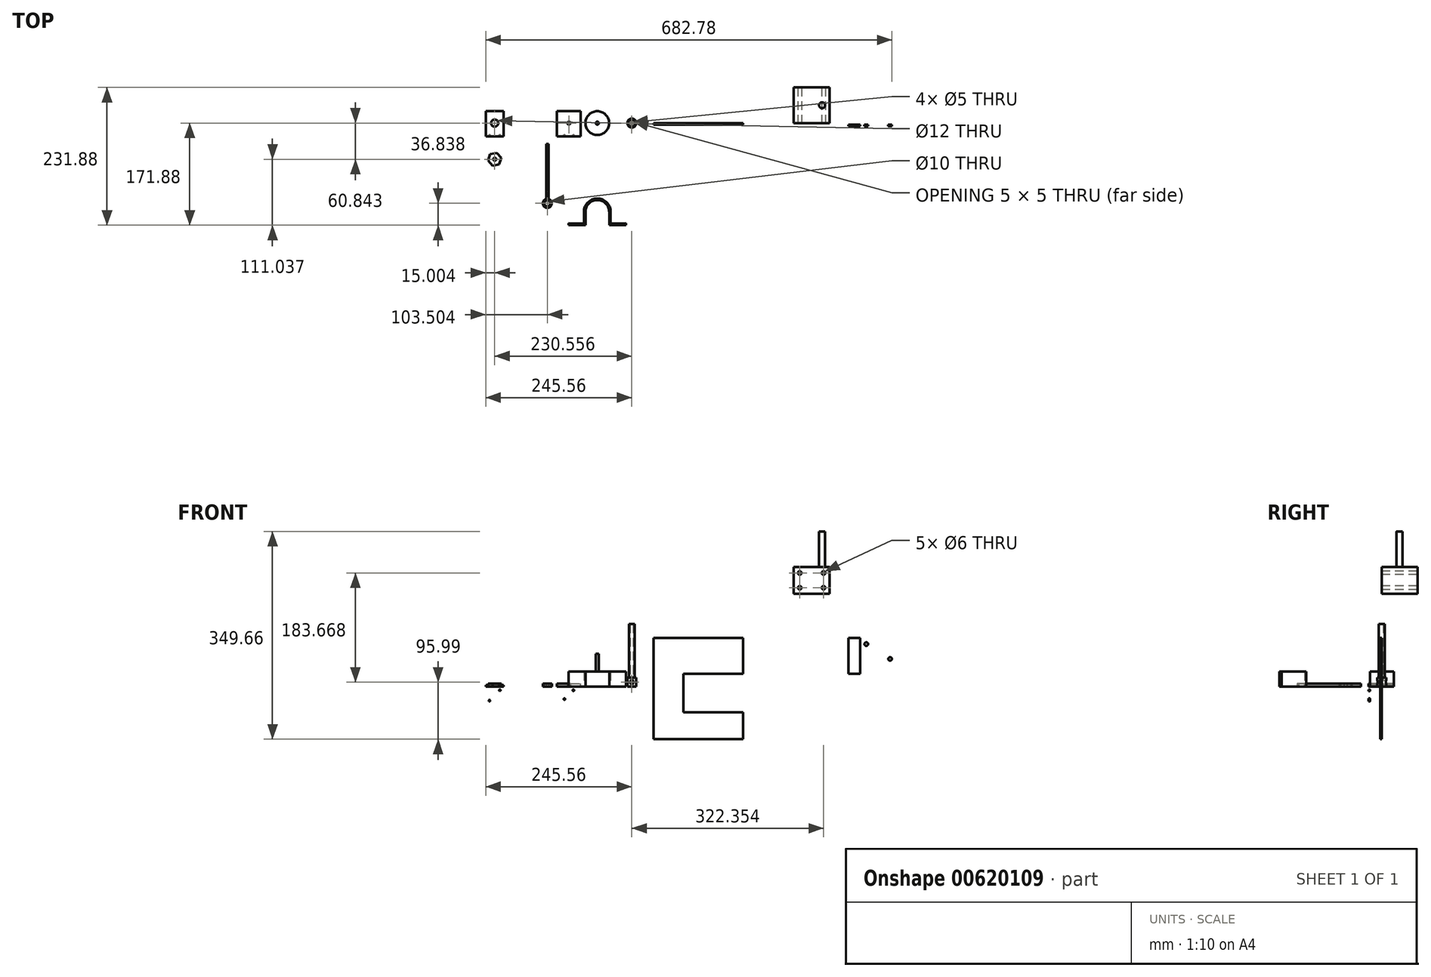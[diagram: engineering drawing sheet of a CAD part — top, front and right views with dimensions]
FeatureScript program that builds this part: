
annotation { "Feature Type Name" : "Feature", "Feature Type Description" : "" }
export const myFeature = defineFeature(function(context is Context, id is Id, definition is map)
    precondition{}
    {
        {
            var Q0;
            Q0=qCreatedBy(makeId("Top.planeOp"),FACE);
            var sketch = newSketch(context, id + "F0", { "sketchPlane" : qUnion([Q0])});
            skCircle(sketch, "E0", {"center": v(0, 0) * mm, "radius": 2.5 * mm});
            skCircle(sketch, "E1", {"center": v(0, 0) * mm, "radius": 7.5 * mm});
            skLineSegment(sketch, "E2", {"start": v(-20, 7.5) * mm, "end": v(20, 7.5) * mm});
            skCircle(sketch, "E3", {"center": v(-57.97, 0) * mm, "radius": 20 * mm});
            skLineSegment(sketch, "E4.bottom", {"start": v(-125.74, 20) * mm, "end": v(-85.74, 20) * mm});
            skLineSegment(sketch, "E4.top", {"start": v(-125.74, -20) * mm, "end": v(-85.74, -20) * mm});
            skLineSegment(sketch, "E4.left", {"start": v(-125.74, 20) * mm, "end": v(-125.74, -20) * mm});
            skLineSegment(sketch, "E4.right", {"start": v(-85.74, 20) * mm, "end": v(-85.74, -20) * mm});
            skPoint(sketch, "E4.middle", {"position": v(-105.74, 0) * mm});
            skCircle(sketch, "E5", {"center": v(-105.74, 0) * mm, "radius": 2.5 * mm});
            skLineSegment(sketch, "E6.bottom", {"start": v(-215.56, 20) * mm, "end": v(-245.56, 20) * mm});
            skLineSegment(sketch, "E6.top", {"start": v(-215.56, -20) * mm, "end": v(-245.56, -20) * mm});
            skLineSegment(sketch, "E6.left", {"start": v(-215.56, 20) * mm, "end": v(-215.56, -20) * mm});
            skLineSegment(sketch, "E6.right", {"start": v(-245.56, 20) * mm, "end": v(-245.56, -20) * mm});
            skCircle(sketch, "E7", {"center": v(-230.56, 0) * mm, "radius": 6 * mm});
            skPoint(sketch, "E7.centerSnap0", {"position": v(-230.56, 20) * mm});
            skCircle(sketch, "E8.cCircle", {"center": v(-230.56, -60.84) * mm, "radius": 9.88 * mm, "construction": true});
            skLineSegment(sketch, "E8.0", {"start": v(-219.4, -58.45) * mm, "end": v(-222.9, -69.3) * mm});
            skLineSegment(sketch, "E8.1", {"start": v(-222.9, -69.3) * mm, "end": v(-234.06, -71.7) * mm});
            skLineSegment(sketch, "E8.2", {"start": v(-234.06, -71.7) * mm, "end": v(-241.71, -63.24) * mm});
            skLineSegment(sketch, "E8.3", {"start": v(-241.71, -63.24) * mm, "end": v(-238.21, -52.38) * mm});
            skLineSegment(sketch, "E8.4", {"start": v(-238.21, -52.38) * mm, "end": v(-227.05, -49.98) * mm});
            skLineSegment(sketch, "E8.5", {"start": v(-227.05, -49.98) * mm, "end": v(-219.4, -58.45) * mm});
            skPoint(sketch, "E8.0.midPoint", {"position": v(-221.15, -63.88) * mm});
            skCircle(sketch, "E9", {"center": v(-230.56, -60.84) * mm, "radius": 2.5 * mm});
            skCircle(sketch, "E10", {"center": v(-142.06, -135.04) * mm, "radius": 5 * mm});
            skArc(sketch, "E11", {"start": v(-144.06, -127.81) * mm, "mid": v(-142.06, -142.54) * mm, "end": v(-140.06, -127.81) * mm});
            skLineSegment(sketch, "E12", {"start": v(-140.06, -127.81) * mm, "end": v(-140.06, -35.04) * mm});
            skLineSegment(sketch, "E13", {"start": v(-140.06, -35.04) * mm, "end": v(-142.06, -35.04) * mm});
            skLineSegment(sketch, "E14.MirrorCS", {"start": v(-144.06, -127.81) * mm, "end": v(-144.06, -35.04) * mm});
            skLineSegment(sketch, "E15", {"start": v(-142.06, -35.04) * mm, "end": v(-144.06, -35.04) * mm});
            skArc(sketch, "E16", {"start": v(-35.47, -149.38) * mm, "mid": v(-57.97, -126.88) * mm, "end": v(-80.47, -149.38) * mm});
            skLineSegment(sketch, "E17", {"start": v(-80.47, -149.38) * mm, "end": v(-80.47, -168.95) * mm});
            skLineSegment(sketch, "E18", {"start": v(-80.47, -171.88) * mm, "end": v(-106.45, -171.88) * mm});
            skLineSegment(sketch, "E19", {"start": v(-106.45, -171.88) * mm, "end": v(-106.45, -168.45) * mm});
            skLineSegment(sketch, "E20", {"start": v(-106.45, -168.45) * mm, "end": v(-80.47, -168.95) * mm});
            skLineSegment(sketch, "E21", {"start": v(-77.97, -149.38) * mm, "end": v(-77.97, -171.88) * mm});
            skLineSegment(sketch, "E22", {"start": v(-77.97, -171.88) * mm, "end": v(-80.47, -171.88) * mm});
            skLineSegment(sketch, "E23.MirrorCS", {"start": v(-37.97, -149.38) * mm, "end": v(-37.97, -171.88) * mm});
            skLineSegment(sketch, "E24.MirrorCS", {"start": v(-35.47, -149.38) * mm, "end": v(-35.47, -168.95) * mm});
            skLineSegment(sketch, "E25.MirrorCS", {"start": v(-9.5, -168.45) * mm, "end": v(-35.47, -168.95) * mm});
            skLineSegment(sketch, "E26.MirrorCS", {"start": v(-9.5, -171.88) * mm, "end": v(-9.5, -168.45) * mm});
            skLineSegment(sketch, "E27.MirrorCS", {"start": v(-35.47, -171.88) * mm, "end": v(-9.5, -171.88) * mm});
            skLineSegment(sketch, "E28.MirrorCS", {"start": v(-37.97, -171.88) * mm, "end": v(-35.47, -171.88) * mm});
            skArc(sketch, "E29.trimOffspring", {"start": v(-37.97, -149.38) * mm, "mid": v(-57.97, -129.38) * mm, "end": v(-77.97, -149.38) * mm});
            skLineSegment(sketch, "E30", {"start": v(-57.97, -130.48) * mm, "end": v(-57.98, -130.48) * mm});
            skLineSegment(sketch, "E31", {"start": v(-57.97, -126.88) * mm, "end": v(-80.26, -126.88) * mm, "construction": true});
            skPoint(sketch, "E32.start.orphan", {"position": v(-57.97, -129.38) * mm});
            skLineSegment(sketch, "E33.MirrorCS", {"start": v(-57.98, -130.48) * mm, "end": v(-57.97, -130.48) * mm});
            skPoint(sketch, "E34.end.orphan", {"position": v(-57.97, -133.51) * mm});
            skLineSegment(sketch, "E35.trimOffspring", {"start": v(-51.44, -130.48) * mm, "end": v(-51.38, -130.48) * mm});
            skSolve(sketch);
        }
        {
            var Q0;
            Q0=makeQuery(id+"F0.imprint","IMPRINT",FACE,{"disambiguationData":[TD([[makeQuery(id+"F0.imprint","IMPRINT",EDGE,{"derivedFrom":sQuery(id+"F0.wireOp",EDGE,"E0")}),-1.0]])]});
            extrude(context, id + "F1", {"entities" : qUnion([Q0]), "depth" : 15 * mm, "offsetDistance" : 25 * mm});
        }
        {
            var Q0;
            Q0=makeQuery(id+"F1.opExtrude","CAP_FACE",FACE,{"disambiguationData":[OSD([sQuery(id+"F0.wireOp",EDGE,"E0"),sQuery(id+"F0.wireOp",EDGE,"E1")])],"isStart":false});
            var sketch = newSketch(context, id + "F2", { "sketchPlane" : qUnion([Q0])});
            skCircle(sketch, "E36", {"center": v(0, 0) * mm, "radius": 5 * mm});
            skSolve(sketch);
        }
        {
            var Q0;
            Q0=makeQuery(id+"F2.imprint","IMPRINT",FACE,{"disambiguationData":[TD([[makeQuery(id+"F2.imprint","IMPRINT",EDGE,{"derivedFrom":sQuery(id+"F2.wireOp",EDGE,"E36")}),1.0]])]});
            extrude(context, id + "F3", {"entities" : qUnion([Q0]), "operationType" : NewBodyOperationType.ADD, "depth" : 90 * mm, "offsetDistance" : 25 * mm});
        }
        {
            var Q0;
            Q0=sQuery(id+"F0.wireOp",EDGE,"E2");
            extrude(context, id + "F4", {"bodyType" : ToolBodyType.SURFACE, "surfaceEntities" : qUnion([Q0]), "depth" : 15 * mm, "offsetDistance" : 25 * mm});
        }
        {
            var Q0;
            Q0=makeQuery(id+"F4.opExtrude","SWEPT_FACE",FACE,{"disambiguationData":[OSD([sQuery(id+"F0.wireOp",EDGE,"E2")])]});
            var sketch = newSketch(context, id + "F5", { "sketchPlane" : qUnion([Q0])});
            skCircle(sketch, "E37", {"center": v(0, 7.5) * mm, "radius": 3 * mm});
            skPoint(sketch, "E37.centerSnap0", {"position": v(-20, 7.5) * mm});
            skSolve(sketch);
        }
        {
            var Q0;
            Q0=makeQuery(id+"F5.imprint","IMPRINT",FACE,{"disambiguationData":[TD([[makeQuery(id+"F5.imprint","IMPRINT",EDGE,{"derivedFrom":sQuery(id+"F5.wireOp",EDGE,"E37")}),1.0]])]});
            extrude(context, id + "F6", {"entities" : qUnion([Q0]), "operationType" : NewBodyOperationType.REMOVE, "endBound" : BoundingType.THROUGH_ALL, "depth" : 25 * mm, "offsetDistance" : 25 * mm});
        }
        {
            var Q0;
            Q0=makeQuery(id+"F0.imprint","IMPRINT",FACE,{"disambiguationData":[TD([[makeQuery(id+"F0.imprint","IMPRINT",EDGE,{"derivedFrom":sQuery(id+"F0.wireOp",EDGE,"E3")}),1.0]])]});
            extrude(context, id + "F7", {"entities" : qUnion([Q0]), "depth" : 25 * mm, "offsetDistance" : 25 * mm});
        }
        {
            var Q0;
            Q0=makeQuery(id+"F7.opExtrude","CAP_FACE",FACE,{"disambiguationData":[OSD([sQuery(id+"F0.wireOp",EDGE,"E3")])],"isStart":false});
            var sketch = newSketch(context, id + "F8", { "sketchPlane" : qUnion([Q0])});
            skCircle(sketch, "E38", {"center": v(-57.97, 0) * mm, "radius": 2.5 * mm});
            skSolve(sketch);
        }
        {
            var Q0;
            Q0=makeQuery(id+"F8.imprint","IMPRINT",FACE,{"disambiguationData":[TD([[makeQuery(id+"F8.imprint","IMPRINT",EDGE,{"derivedFrom":sQuery(id+"F8.wireOp",EDGE,"E38")}),1.0]])]});
            extrude(context, id + "F9", {"entities" : qUnion([Q0]), "operationType" : NewBodyOperationType.ADD, "depth" : 30 * mm, "offsetDistance" : 25 * mm});
        }
        {
            var Q0;
            Q0=makeQuery(id+"F0.imprint","IMPRINT",FACE,{"disambiguationData":[TD([[makeQuery(id+"F0.imprint","IMPRINT",EDGE,{"derivedFrom":sQuery(id+"F0.wireOp",EDGE,"E4.bottom")}),-1.0]])]});
            extrude(context, id + "F10", {"entities" : qUnion([Q0]), "depth" : 5 * mm, "offsetDistance" : 25 * mm});
        }
        {
            var Q0;
            Q0=makeQuery(id+"F10.opExtrude","CAP_FACE",FACE,{"disambiguationData":[OSD([sQuery(id+"F0.wireOp",EDGE,"E4.bottom"),sQuery(id+"F0.wireOp",EDGE,"E4.top"),sQuery(id+"F0.wireOp",EDGE,"E4.left"),sQuery(id+"F0.wireOp",EDGE,"E4.right"),sQuery(id+"F0.wireOp",EDGE,"E5")])],"isStart":false});
            var sketch = newSketch(context, id + "F11", { "sketchPlane" : qUnion([Q0])});
            skLineSegment(sketch, "E39.bottom", {"start": v(-125.74, -20) * mm, "end": v(-85.74, -20) * mm});
            skLineSegment(sketch, "E39.top", {"start": v(-125.74, -22.5) * mm, "end": v(-85.74, -22.5) * mm});
            skLineSegment(sketch, "E39.left", {"start": v(-125.74, -20) * mm, "end": v(-125.74, -22.5) * mm});
            skLineSegment(sketch, "E39.right", {"start": v(-85.74, -20) * mm, "end": v(-85.74, -22.5) * mm});
            skSolve(sketch);
        }
        {
            var Q0;
            Q0=makeQuery(id+"F11.imprint","IMPRINT",FACE,{"disambiguationData":[TD([[makeQuery(id+"F11.imprint","IMPRINT",EDGE,{"derivedFrom":sQuery(id+"F11.wireOp",EDGE,"E39.bottom")}),-1.0]])]});
            extrude(context, id + "F12", {"entities" : qUnion([Q0]), "operationType" : NewBodyOperationType.ADD, "oppositeDirection" : true, "depth" : 32.5 * mm, "offsetDistance" : 25 * mm});
        }
        {
            var Q0;
            Q0=qCreatedBy(makeId("Front.planeOp"),FACE);
            var sketch = newSketch(context, id + "F13", { "sketchPlane" : qUnion([Q0])});
            skLineSegment(sketch, "E40.bottom", {"start": v(36.88, 81.5) * mm, "end": v(186.88, 81.5) * mm});
            skLineSegment(sketch, "E40.top", {"start": v(36.88, -88.5) * mm, "end": v(186.88, -88.5) * mm});
            skLineSegment(sketch, "E40.left", {"start": v(36.88, 81.5) * mm, "end": v(36.88, -88.5) * mm});
            skLineSegment(sketch, "E40.right", {"start": v(186.88, 81.5) * mm, "end": v(186.88, -88.5) * mm});
            skLineSegment(sketch, "E41", {"start": v(186.88, 21.5) * mm, "end": v(86.88, 21.5) * mm});
            skLineSegment(sketch, "E42", {"start": v(186.88, -43.5) * mm, "end": v(86.88, -43.5) * mm});
            skLineSegment(sketch, "E43", {"start": v(86.88, 21.5) * mm, "end": v(86.88, -43.5) * mm});
            skLineSegment(sketch, "E44.bottom", {"start": v(272.35, 201.17) * mm, "end": v(332.35, 201.17) * mm});
            skLineSegment(sketch, "E44.top", {"start": v(272.35, 156.17) * mm, "end": v(332.35, 156.17) * mm});
            skLineSegment(sketch, "E44.left", {"start": v(272.35, 201.17) * mm, "end": v(272.35, 156.17) * mm});
            skLineSegment(sketch, "E44.right", {"start": v(332.35, 201.17) * mm, "end": v(332.35, 156.17) * mm});
            skCircle(sketch, "E45", {"center": v(322.35, 191.17) * mm, "radius": 3 * mm});
            skLineSegment(sketch, "E46", {"start": v(272.35, 178.67) * mm, "end": v(332.35, 178.67) * mm, "construction": true});
            skLineSegment(sketch, "E47", {"start": v(302.35, 156.17) * mm, "end": v(302.35, 201.17) * mm, "construction": true});
            skCircle(sketch, "E48.MirrorC", {"center": v(282.35, 191.17) * mm, "radius": 3 * mm});
            skCircle(sketch, "E49.MirrorC", {"center": v(282.35, 166.17) * mm, "radius": 3 * mm});
            skCircle(sketch, "E50.MirrorC", {"center": v(322.35, 166.17) * mm, "radius": 3 * mm});
            skSolve(sketch);
        }
        {
            var Q0;
            {var subQ1=sQuery(id+"F13.wireOp",EDGE,"E40.bottom");Q0=makeQuery(id+"F13.imprint","IMPRINT",FACE,{"disambiguationData":[TD([[makeQuery(id+"F13.imprint","IMPRINT",EDGE,{"derivedFrom":subQ1}),-1.0]])]});}
            extrude(context, id + "F14", {"entities" : qUnion([Q0]), "depth" : 2.5 * mm, "offsetDistance" : 25 * mm});
        }
        {
            var Q0;
            Q0=makeQuery(id+"F14.opExtrude","CAP_FACE",FACE,{"disambiguationData":[OSD([sQuery(id+"F13.wireOp",EDGE,"E40.bottom"),sQuery(id+"F13.wireOp",EDGE,"E40.top"),sQuery(id+"F13.wireOp",EDGE,"E40.left"),sQuery(id+"F13.wireOp",EDGE,"E40.right"),sQuery(id+"F13.wireOp",EDGE,"E41"),sQuery(id+"F13.wireOp",EDGE,"E42"),sQuery(id+"F13.wireOp",EDGE,"E43")])],"isStart":false});
            var sketch = newSketch(context, id + "F15", { "sketchPlane" : qUnion([Q0])});
            skLineSegment(sketch, "E51", {"start": v(186.88, 49) * mm, "end": v(86.88, 49) * mm});
            skLineSegment(sketch, "E52", {"start": v(86.88, 49) * mm, "end": v(86.88, 21.5) * mm});
            skLineSegment(sketch, "E53", {"start": v(186.88, -43.5) * mm, "end": v(86.88, -43.5) * mm});
            skLineSegment(sketch, "E54", {"start": v(86.88, -43.5) * mm, "end": v(86.88, -43.5) * mm});
            skLineSegment(sketch, "E55", {"start": v(86.88, 49) * mm, "end": v(86.88, 81.5) * mm});
            skLineSegment(sketch, "E56", {"start": v(86.88, 81.5) * mm, "end": v(86.88, -88.5) * mm});
            skLineSegment(sketch, "E57.bottom", {"start": v(364.22, 81.5) * mm, "end": v(444.22, 81.5) * mm});
            skLineSegment(sketch, "E57.top", {"start": v(384.22, 36.5) * mm, "end": v(444.22, 36.5) * mm});
            skLineSegment(sketch, "E57.right", {"start": v(444.22, 81.5) * mm, "end": v(444.22, 36.5) * mm});
            skLineSegment(sketch, "E58", {"start": v(384.22, 36.5) * mm, "end": v(384.22, 21.5) * mm});
            skLineSegment(sketch, "E59", {"start": v(384.22, 21.5) * mm, "end": v(364.22, 21.5) * mm});
            skLineSegment(sketch, "E60", {"start": v(364.22, 81.5) * mm, "end": v(364.22, 21.5) * mm});
            skSolve(sketch);
        }
        {
            var Q0;
            Q0=makeQuery(id+"F0.imprint","IMPRINT",FACE,{"disambiguationData":[TD([[makeQuery(id+"F0.imprint","IMPRINT",EDGE,{"derivedFrom":sQuery(id+"F0.wireOp",EDGE,"E6.bottom")}),1.0]])]});
            extrude(context, id + "F16", {"entities" : qUnion([Q0]), "depth" : 2.5 * mm, "offsetDistance" : 25 * mm});
        }
        {
            var Q0;
            Q0=makeQuery(id+"F16.opExtrude","CAP_FACE",FACE,{"disambiguationData":[OSD([sQuery(id+"F0.wireOp",EDGE,"E6.bottom"),sQuery(id+"F0.wireOp",EDGE,"E6.top"),sQuery(id+"F0.wireOp",EDGE,"E6.left"),sQuery(id+"F0.wireOp",EDGE,"E6.right"),sQuery(id+"F0.wireOp",EDGE,"E7")])],"isStart":false});
            var sketch = newSketch(context, id + "F17", { "sketchPlane" : qUnion([Q0])});
            skLineSegment(sketch, "E61.bottom", {"start": v(-245.56, -20) * mm, "end": v(-215.56, -20) * mm});
            skLineSegment(sketch, "E61.top", {"start": v(-245.56, -22.5) * mm, "end": v(-215.56, -22.5) * mm});
            skLineSegment(sketch, "E61.left", {"start": v(-245.56, -20) * mm, "end": v(-245.56, -22.5) * mm});
            skLineSegment(sketch, "E61.right", {"start": v(-215.56, -20) * mm, "end": v(-215.56, -22.5) * mm});
            skSolve(sketch);
        }
        {
            var Q0;
            Q0=makeQuery(id+"F17.imprint","IMPRINT",FACE,{"disambiguationData":[TD([[makeQuery(id+"F17.imprint","IMPRINT",EDGE,{"derivedFrom":sQuery(id+"F17.wireOp",EDGE,"E61.bottom")}),1.0]])]});
            extrude(context, id + "F18", {"entities" : qUnion([Q0]), "operationType" : NewBodyOperationType.ADD, "oppositeDirection" : true, "depth" : 32.5 * mm, "offsetDistance" : 25 * mm});
        }
        {
            var Q0;
            Q0=makeQuery(id+"F0.imprint","IMPRINT",FACE,{"disambiguationData":[TD([[makeQuery(id+"F0.imprint","IMPRINT",EDGE,{"derivedFrom":sQuery(id+"F0.wireOp",EDGE,"E8.0")}),-1.0]])]});
            extrude(context, id + "F19", {"entities" : qUnion([Q0]), "depth" : 5 * mm, "offsetDistance" : 25 * mm});
        }
        {
            var Q0;
            Q0=makeQuery(id+"F12.opExtrude","SWEPT_FACE",FACE,{"disambiguationData":[OSD([sQuery(id+"F11.wireOp",EDGE,"E39.bottom")])]});
            var sketch = newSketch(context, id + "F20", { "sketchPlane" : qUnion([Q0])});
            skCircle(sketch, "E62", {"center": v(113.24, -6.25) * mm, "radius": 1.25 * mm});
            skLineSegment(sketch, "E63", {"start": v(105.74, 0) * mm, "end": v(105.74, -27.5) * mm, "construction": true});
            skLineSegment(sketch, "E64", {"start": v(125.74, -13.75) * mm, "end": v(85.74, -13.75) * mm, "construction": true});
            skCircle(sketch, "E65.MirrorC", {"center": v(98.24, -6.25) * mm, "radius": 1.25 * mm});
            skCircle(sketch, "E66.MirrorC", {"center": v(98.24, -21.25) * mm, "radius": 1.25 * mm});
            skCircle(sketch, "E67.MirrorC", {"center": v(113.24, -21.25) * mm, "radius": 1.25 * mm});
            skSolve(sketch);
        }
        {
            var Q0;
            Q0=makeQuery(id+"F20.imprint","IMPRINT",FACE,{"disambiguationData":[TD([[makeQuery(id+"F20.imprint","IMPRINT",EDGE,{"derivedFrom":sQuery(id+"F20.wireOp",EDGE,"E65.MirrorC")}),-1.0]])]});
            var Q1;
            Q1=makeQuery(id+"F20.imprint","IMPRINT",FACE,{"disambiguationData":[TD([[makeQuery(id+"F20.imprint","IMPRINT",EDGE,{"derivedFrom":sQuery(id+"F20.wireOp",EDGE,"E62")}),1.0]])]});
            var Q2;
            Q2=makeQuery(id+"F20.imprint","IMPRINT",FACE,{"disambiguationData":[TD([[makeQuery(id+"F20.imprint","IMPRINT",EDGE,{"derivedFrom":sQuery(id+"F20.wireOp",EDGE,"E67.MirrorC")}),-1.0]])]});
            var Q3;
            Q3=makeQuery(id+"F20.imprint","IMPRINT",FACE,{"disambiguationData":[TD([[makeQuery(id+"F20.imprint","IMPRINT",EDGE,{"derivedFrom":sQuery(id+"F20.wireOp",EDGE,"E66.MirrorC")}),1.0]])]});
            extrude(context, id + "F21", {"entities" : qUnion([Q0, Q1, Q2, Q3]), "operationType" : NewBodyOperationType.REMOVE, "endBound" : BoundingType.UP_TO_NEXT, "oppositeDirection" : true, "depth" : 25 * mm, "offsetDistance" : 25 * mm});
        }
        {
            var Q0;
            Q0=makeQuery(id+"F18.opExtrude","SWEPT_FACE",FACE,{"disambiguationData":[OSD([sQuery(id+"F17.wireOp",EDGE,"E61.bottom")])]});
            var sketch = newSketch(context, id + "F22", { "sketchPlane" : qUnion([Q0])});
            skLineSegment(sketch, "E68", {"start": v(230.56, 0) * mm, "end": v(230.56, -30) * mm, "construction": true});
            skLineSegment(sketch, "E69", {"start": v(215.56, -15) * mm, "end": v(245.56, -15) * mm, "construction": true});
            skCircle(sketch, "E70", {"center": v(239.3, -6.25) * mm, "radius": 1.25 * mm});
            skCircle(sketch, "E71.MirrorC", {"center": v(221.8, -6.25) * mm, "radius": 1.25 * mm});
            skCircle(sketch, "E72.MirrorC", {"center": v(221.8, -23.75) * mm, "radius": 1.25 * mm});
            skCircle(sketch, "E73.MirrorC", {"center": v(239.3, -23.75) * mm, "radius": 1.25 * mm});
            skSolve(sketch);
        }
        {
            var Q0;
            Q0=makeQuery(id+"F22.imprint","IMPRINT",FACE,{"disambiguationData":[TD([[makeQuery(id+"F22.imprint","IMPRINT",EDGE,{"derivedFrom":sQuery(id+"F22.wireOp",EDGE,"E71.MirrorC")}),-1.0]])]});
            var Q1;
            Q1=makeQuery(id+"F22.imprint","IMPRINT",FACE,{"disambiguationData":[TD([[makeQuery(id+"F22.imprint","IMPRINT",EDGE,{"derivedFrom":sQuery(id+"F22.wireOp",EDGE,"E72.MirrorC")}),1.0]])]});
            var Q2;
            Q2=makeQuery(id+"F22.imprint","IMPRINT",FACE,{"disambiguationData":[TD([[makeQuery(id+"F22.imprint","IMPRINT",EDGE,{"derivedFrom":sQuery(id+"F22.wireOp",EDGE,"E73.MirrorC")}),-1.0]])]});
            var Q3;
            Q3=makeQuery(id+"F22.imprint","IMPRINT",FACE,{"disambiguationData":[TD([[makeQuery(id+"F22.imprint","IMPRINT",EDGE,{"derivedFrom":sQuery(id+"F22.wireOp",EDGE,"E70")}),1.0]])]});
            extrude(context, id + "F23", {"entities" : qUnion([Q0, Q1, Q2, Q3]), "operationType" : NewBodyOperationType.REMOVE, "endBound" : BoundingType.UP_TO_NEXT, "oppositeDirection" : true, "depth" : 25 * mm, "offsetDistance" : 25 * mm});
        }
        {
            var Q0;
            Q0=makeQuery(id+"F13.imprint","IMPRINT",FACE,{"disambiguationData":[TD([[makeQuery(id+"F13.imprint","IMPRINT",EDGE,{"derivedFrom":sQuery(id+"F13.wireOp",EDGE,"E44.bottom")}),-1.0]])]});
            extrude(context, id + "F24", {"entities" : qUnion([Q0]), "oppositeDirection" : true, "depth" : 60 * mm, "offsetDistance" : 25 * mm});
        }
        {
            var Q0;
            Q0=makeQuery(id+"F24.opExtrude","SWEPT_FACE",FACE,{"disambiguationData":[OSD([sQuery(id+"F13.wireOp",EDGE,"E44.bottom")])]});
            var sketch = newSketch(context, id + "F25", { "sketchPlane" : qUnion([Q0])});
            skCircle(sketch, "E74", {"center": v(319.85, 30) * mm, "radius": 5 * mm});
            skCircle(sketch, "E75", {"center": v(319.85, 30) * mm, "radius": 12.5 * mm, "construction": true});
            skSolve(sketch);
        }
        {
            var Q0;
            Q0=makeQuery(id+"F25.imprint","IMPRINT",FACE,{"disambiguationData":[TD([[makeQuery(id+"F25.imprint","IMPRINT",EDGE,{"derivedFrom":sQuery(id+"F25.wireOp",EDGE,"E74")}),1.0]])]});
            extrude(context, id + "F26", {"entities" : qUnion([Q0]), "operationType" : NewBodyOperationType.ADD, "depth" : 60 * mm, "offsetDistance" : 25 * mm});
        }
        {
            var Q0;
            Q0=makeQuery(id+"F15.imprint","IMPRINT",FACE,{"disambiguationData":[TD([[makeQuery(id+"F15.imprint","IMPRINT",EDGE,{"derivedFrom":sQuery(id+"F15.wireOp",EDGE,"E57.bottom")}),-1.0]])]});
            extrude(context, id + "F27", {"entities" : qUnion([Q0]), "depth" : 2.5 * mm, "offsetDistance" : 25 * mm});
        }
        {
            var Q0;
            Q0=makeQuery(id+"F27.opExtrude","CAP_FACE",FACE,{"disambiguationData":[OSD([sQuery(id+"F15.wireOp",EDGE,"E57.bottom"),sQuery(id+"F15.wireOp",EDGE,"E57.top"),sQuery(id+"F15.wireOp",EDGE,"E57.left"),sQuery(id+"F15.wireOp",EDGE,"E57.right")])],"isStart":false});
            var sketch = newSketch(context, id + "F28", { "sketchPlane" : qUnion([Q0])});
            skLineSegment(sketch, "E76", {"start": v(384.22, 81.5) * mm, "end": v(384.22, 36.5) * mm});
            skLineSegment(sketch, "E77", {"start": v(414.22, 36.5) * mm, "end": v(414.22, 81.5) * mm, "construction": true});
            skLineSegment(sketch, "E78", {"start": v(444.22, 59) * mm, "end": v(384.22, 59) * mm, "construction": true});
            skCircle(sketch, "E79", {"center": v(434.22, 71.5) * mm, "radius": 3 * mm});
            skCircle(sketch, "E80.MirrorC", {"center": v(394.22, 71.5) * mm, "radius": 3 * mm});
            skCircle(sketch, "E81.MirrorC", {"center": v(394.22, 46.5) * mm, "radius": 3 * mm});
            skCircle(sketch, "E82.MirrorC", {"center": v(434.22, 46.5) * mm, "radius": 3 * mm});
            skSolve(sketch);
        }
        {
            var Q0;
            Q0=makeQuery(id+"F28.imprint","IMPRINT",FACE,{"disambiguationData":[TD([[makeQuery(id+"F28.imprint","IMPRINT",EDGE,{"derivedFrom":sQuery(id+"F28.wireOp",EDGE,"E80.MirrorC")}),-1.0]])]});
            var Q1;
            Q1=makeQuery(id+"F28.imprint","IMPRINT",FACE,{"disambiguationData":[TD([[makeQuery(id+"F28.imprint","IMPRINT",EDGE,{"derivedFrom":sQuery(id+"F28.wireOp",EDGE,"E81.MirrorC")}),1.0]])]});
            var Q2;
            Q2=makeQuery(id+"F28.imprint","IMPRINT",FACE,{"disambiguationData":[TD([[makeQuery(id+"F28.imprint","IMPRINT",EDGE,{"derivedFrom":sQuery(id+"F28.wireOp",EDGE,"E79")}),1.0]])]});
            var Q3;
            Q3=makeQuery(id+"F28.imprint","IMPRINT",FACE,{"disambiguationData":[TD([[makeQuery(id+"F28.imprint","IMPRINT",EDGE,{"derivedFrom":sQuery(id+"F28.wireOp",EDGE,"E82.MirrorC")}),-1.0]])]});
            extrude(context, id + "F29", {"entities" : qUnion([Q0, Q1, Q2, Q3]), "operationType" : NewBodyOperationType.REMOVE, "oppositeDirection" : true, "depth" : 25 * mm, "offsetDistance" : 25 * mm});
        }
        {
            var Q0;
            Q0=makeQuery(id+"F0.imprint","IMPRINT",FACE,{"disambiguationData":[TD([[makeQuery(id+"F0.imprint","IMPRINT",EDGE,{"derivedFrom":sQuery(id+"F0.wireOp",EDGE,"E10")}),-1.0]])]});
            extrude(context, id + "F30", {"entities" : qUnion([Q0]), "depth" : 5 * mm, "offsetDistance" : 25 * mm});
        }
        {
            var Q0;
            Q0=makeQuery(id+"F0.imprint","IMPRINT",FACE,{"disambiguationData":[TD([[makeQuery(id+"F0.imprint","IMPRINT",EDGE,{"derivedFrom":sQuery(id+"F0.wireOp",EDGE,"E16")}),1.0]])]});
            var Q1;
            {var subQ0=sQuery(id+"F0.wireOp",EDGE,"E30");Q1=makeQuery(id+"F0.imprint","IMPRINT",FACE,{"disambiguationData":[TD([[makeQuery(id+"F0.imprint","IMPRINT",EDGE,{"derivedFrom":subQ0}),-1.0]])]});}
            extrude(context, id + "F31", {"entities" : qUnion([Q0, Q1]), "depth" : 25 * mm, "offsetDistance" : 25 * mm});
        }
    });
